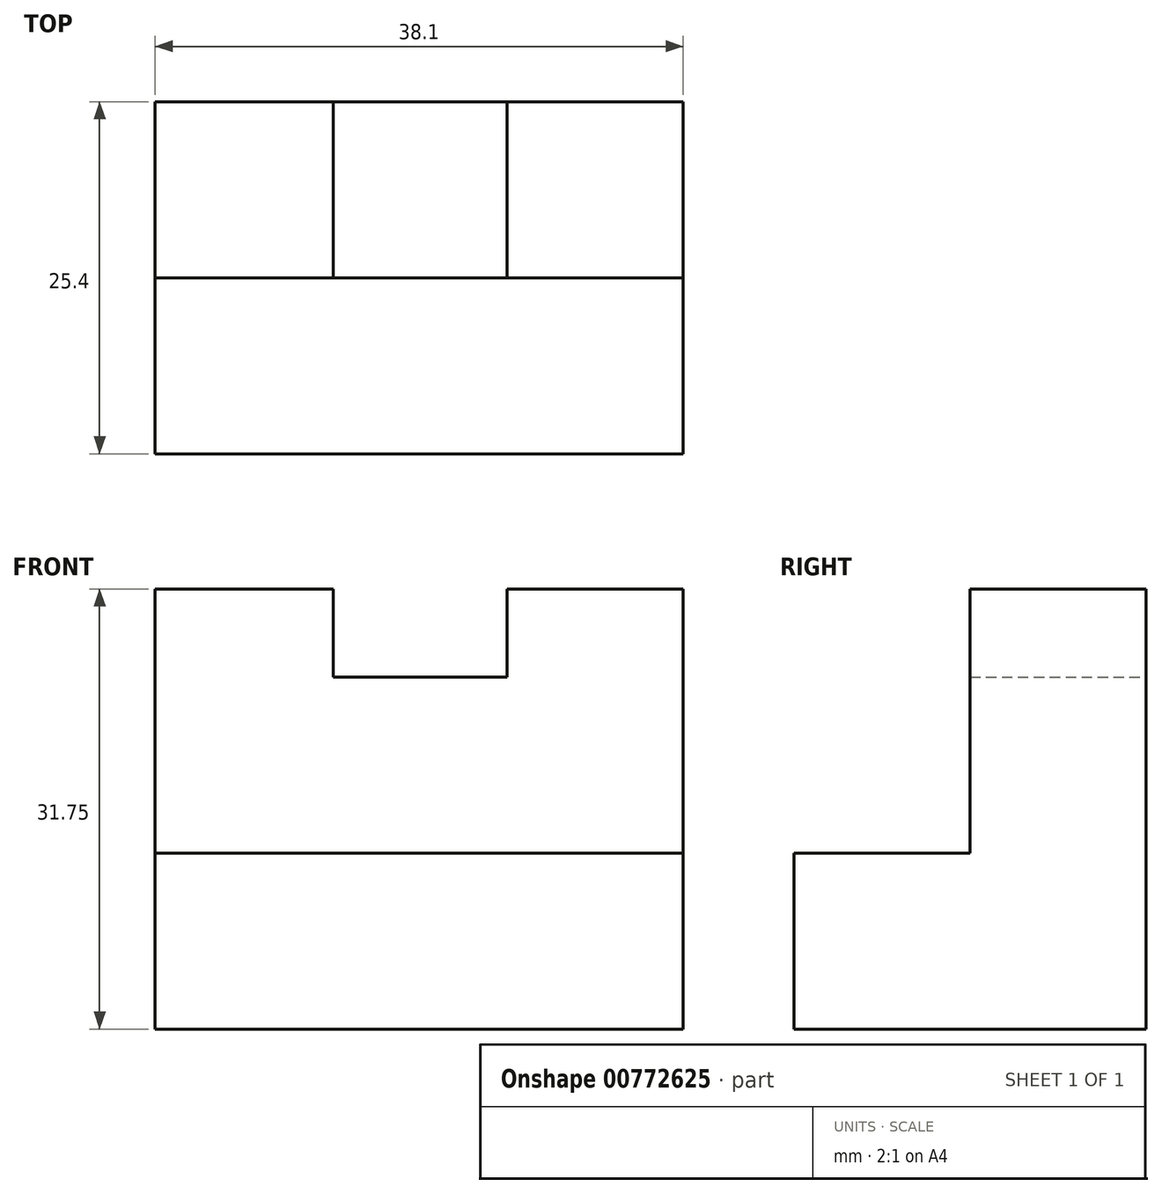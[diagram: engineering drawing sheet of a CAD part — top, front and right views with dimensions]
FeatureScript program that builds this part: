
annotation { "Feature Type Name" : "Feature", "Feature Type Description" : "" }
export const myFeature = defineFeature(function(context is Context, id is Id, definition is map)
    precondition{}
    {
        {
            var Q0;
            Q0=qCreatedBy(makeId("Right.planeOp"),FACE);
            var sketch = newSketch(context, id + "F0", { "sketchPlane" : qUnion([Q0])});
            skLineSegment(sketch, "E0", {"start": v(0, 0) * mm, "end": v(25.4, 0) * mm});
            skLineSegment(sketch, "E1", {"start": v(25.4, 0) * mm, "end": v(25.4, 31.75) * mm});
            skLineSegment(sketch, "E2", {"start": v(25.4, 31.75) * mm, "end": v(12.7, 31.75) * mm});
            skLineSegment(sketch, "E3", {"start": v(12.7, 31.75) * mm, "end": v(12.7, 12.7) * mm});
            skLineSegment(sketch, "E4", {"start": v(12.7, 12.7) * mm, "end": v(0, 12.7) * mm});
            skLineSegment(sketch, "E5", {"start": v(0, 12.7) * mm, "end": v(0, 0) * mm});
            skSolve(sketch);
        }
        {
            var Q0;
            Q0=makeQuery(id+"F0.imprint","IMPRINT",FACE,{"disambiguationData":[TD([[makeQuery(id+"F0.imprint","IMPRINT",EDGE,{"derivedFrom":sQuery(id+"F0.wireOp",EDGE,"E0")}),1.0]])]});
            extrude(context, id + "F1", {"entities" : qUnion([Q0]), "depth" : 38.1 * mm, "offsetDistance" : 25.4 * mm});
        }
        {
            var Q0;
            Q0=makeQuery(id+"F1.opExtrude","SWEPT_FACE",FACE,{"disambiguationData":[OSD([sQuery(id+"F0.wireOp",EDGE,"E3")])]});
            var sketch = newSketch(context, id + "F2", { "sketchPlane" : qUnion([Q0])});
            skLineSegment(sketch, "E6", {"start": v(0, 31.75) * mm, "end": v(12.7, 31.75) * mm});
            skLineSegment(sketch, "E7", {"start": v(38.1, 31.75) * mm, "end": v(25.4, 31.75) * mm});
            skSolve(sketch);
        }
        {
            var Q0;
            Q0=makeQuery(id+"F1.opExtrude","SWEPT_FACE",FACE,{"disambiguationData":[OSD([sQuery(id+"F0.wireOp",EDGE,"E2")])]});
            var sketch = newSketch(context, id + "F3", { "sketchPlane" : qUnion([Q0])});
            skLineSegment(sketch, "E8", {"start": v(12.84, 12.7) * mm, "end": v(12.84, 25.4) * mm});
            skLineSegment(sketch, "E9", {"start": v(25.4, 12.7) * mm, "end": v(25.4, 25.4) * mm});
            skSolve(sketch);
        }
        {
            var Q0;
            {var subQ0=sQuery(id+"F3.wireOp",EDGE,"E8");Q0=makeQuery(id+"F3.imprint","IMPRINT",FACE,{"disambiguationData":[TD([[makeQuery(id+"F3.imprint","IMPRINT",EDGE,{"derivedFrom":subQ0}),-1.0]])]});}
            extrude(context, id + "F4", {"entities" : qUnion([Q0]), "operationType" : NewBodyOperationType.REMOVE, "oppositeDirection" : true, "depth" : 6.35 * mm, "offsetDistance" : 25.4 * mm});
        }
    });
